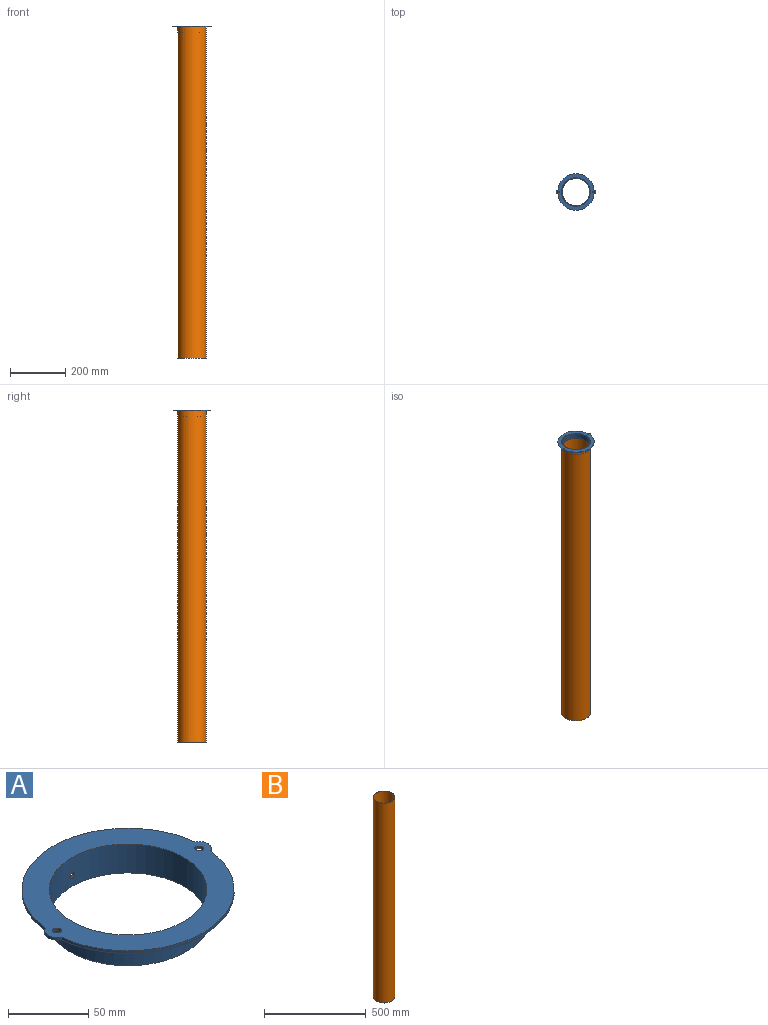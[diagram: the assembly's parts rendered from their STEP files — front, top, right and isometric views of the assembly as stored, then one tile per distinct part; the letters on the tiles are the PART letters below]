
ASSEMBLY  parts=2 mates=1
PART A: 13 faces, bbox 140x132x22 mm
  f0: cylinder r=66mm len=131.3mm, axis (0,0,-1), area 387.4mm2, adj f3,f4,f7,f8
  f1: cylinder r=66mm len=131.3mm, axis (0,0,-1), area 387.4mm2, adj f3,f4,f7,f8
  f2: cylinder r=49mm len=98mm, axis (0,0,-1), area 6744.9mm2, adj f3,f6,f11,f12
  f3: plane 140x132mm, normal (0,0,1), area 6177.3mm2, adj f0,f1,f2,f7,f8,f9,f10
  f4: plane 140x132mm, normal (0,0,-1), area 5548.9mm2, adj f0,f1,f5,f7,f8,f9,f10
  f5: cylinder r=51mm len=102mm, axis (0,0,-1), area 6380.4mm2, adj f4,f6,f11,f12
  f6: plane 102x102mm, normal (0,0,-1), area 628.3mm2, adj f2,f5
  f7: cylinder r=7.5mm len=13.61mm, axis (0,0,-1), area 34.1mm2, adj f0,f1,f3,f4
  f8: cylinder r=7.5mm len=13.61mm, axis (0,0,-1), area 34.1mm2, adj f0,f1,f3,f4
  f9: cylinder r=2.62mm len=5.25mm, axis (0,0,-1), area 33mm2, adj f3,f4
  f10: cylinder r=2.62mm len=5.25mm, axis (0,0,-1), area 33mm2, adj f3,f4
  f11: cylinder r=2.12mm len=4.25mm, axis (0,-1,0), area 26.7mm2, adj f2,f5
  f12: cylinder r=2.12mm len=4.25mm, axis (0,-1,0), area 26.7mm2, adj f2,f5
PART B: 4 faces, bbox 104x104x1200 mm
  f0: cylinder r=52mm len=1200mm, axis (0,0,1), area 392070.8mm2, adj f1,f2
  f1: plane 104x104mm, normal (0,0,1), area 323.6mm2, adj f0,f3
  f2: plane 104x104mm, normal (0,0,-1), area 323.6mm2, adj f0,f3
  f3: cylinder r=51mm len=1200mm, axis (0,0,1), area 384530.9mm2, adj f1,f2
PLACE A t=(239.33,201.58,94.11)mm
PLACE B t=(239.33,201.58,-504.89)mm
MATE fastened B.f0 <-> A.f0  axis (0,0,1) through (239.33,201.58,96.11)mm
